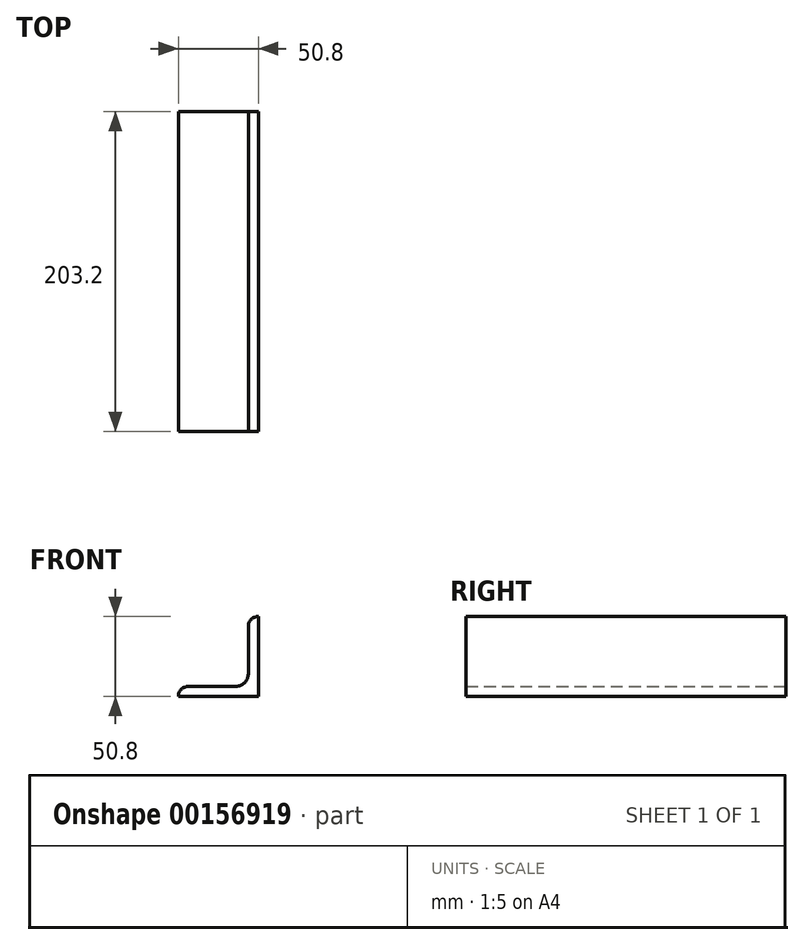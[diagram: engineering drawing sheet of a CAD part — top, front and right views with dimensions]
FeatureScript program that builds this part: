
annotation { "Feature Type Name" : "Feature", "Feature Type Description" : "" }
export const myFeature = defineFeature(function(context is Context, id is Id, definition is map)
    precondition{}
    {
        {
            var Q0;
            Q0=qCreatedBy(makeId("Front.planeOp"),FACE);
            var sketch = newSketch(context, id + "F0", { "sketchPlane" : qUnion([Q0])});
            skLineSegment(sketch, "E0", {"start": v(0, 0) * mm, "end": v(50.8, 0) * mm});
            skLineSegment(sketch, "E1", {"start": v(50.8, 0) * mm, "end": v(50.8, 50.8) * mm});
            skLineSegment(sketch, "E2", {"start": v(0, 0) * mm, "end": v(0, 0) * mm});
            skLineSegment(sketch, "E3", {"start": v(50.8, 50.8) * mm, "end": v(50.8, 50.8) * mm});
            skLineSegment(sketch, "E4", {"start": v(44.45, 44.45) * mm, "end": v(44.45, 14.29) * mm});
            skLineSegment(sketch, "E5", {"start": v(6.35, 6.35) * mm, "end": v(36.51, 6.35) * mm});
            skPoint(sketch, "E6.visualSharp", {"position": v(44.45, 50.8) * mm});
            skArc(sketch, "E6.filletArc", {"start": v(50.8, 50.8) * mm, "mid": v(46.3, 48.94) * mm, "end": v(44.45, 44.45) * mm});
            skPoint(sketch, "E7.visualSharp", {"position": v(0, 6.35) * mm});
            skArc(sketch, "E7.filletArc", {"start": v(6.35, 6.35) * mm, "mid": v(1.86, 4.5) * mm, "end": v(0, 0) * mm});
            skPoint(sketch, "E8.visualSharp", {"position": v(44.45, 6.35) * mm});
            skArc(sketch, "E8.filletArc", {"start": v(36.51, 6.35) * mm, "mid": v(42.13, 8.67) * mm, "end": v(44.45, 14.29) * mm});
            skSolve(sketch);
        }
        {
            var Q0;
            Q0=makeQuery(id+"F0.imprint","IMPRINT",FACE,{"disambiguationData":[TD([[makeQuery(id+"F0.imprint","IMPRINT",EDGE,{"derivedFrom":sQuery(id+"F0.wireOp",EDGE,"E0")}),1.0]])]});
            extrude(context, id + "F1", {"entities" : qUnion([Q0]), "depth" : 203.2 * mm});
        }
    });
